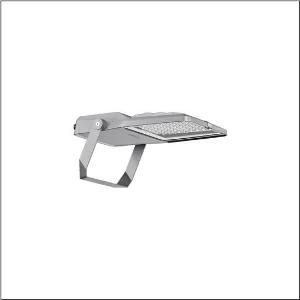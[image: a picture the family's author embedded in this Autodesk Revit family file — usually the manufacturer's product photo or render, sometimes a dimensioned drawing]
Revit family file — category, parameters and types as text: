
# Revit family: floodlight_fl_21_iq_mini___pl52_5xa7772c2d1a_8042
name_source: partatom
category: Lighting Fixtures
units: mm (PartAtom-declared; Revit-internal decimal feet)

## family parameters
Cut with Voids When Loaded = No
Host = Face
Light Source = No
Part Type = Normal
Room Calculation Point = No
Round Connector Dimension = Use Diameter
Shared = No

## types (1)
- --- (1 x LED, 12210 lm, 87.2 W, 3000K)
    Apparent Load = 87 VA
    CIE Flux Codes = 26 60 98 100 100
    Color Rendering = 70
    Color Temperature = 3000K
    Default Elevation = 1800 mm
    Description = Floodlight FL 21 iQ mini, floodlight, primary light control with lens, of PMMA, primary optical cover: protective disc, of toughened safety glass, transparent, light distribution: PL52, light emission: direct distribution, installation type: surface-mounted, LED, High Power LED, rated luminous flux: 12.210lm, luminous efficacy: 140lm/W, light colour: 730, colour temperature: 3000K, control: Street-Remote, Auto-Match, Temp-Guard, Night-Set, Smart-Wire, Desk-Remote (wireless, voltage-free reading and setting of iQ features in the workshop via application-optimized NFC function/RFID function), optimised constant luminous flux control (CLO 2.0), with terminal, 6-pole, mains connection: 220..240V, AC, 50/60Hz, start of lifetime: 87W, end of service life: 92W, reduction: 40W, luminaire housing, of diecast aluminium, powder-coated, Siteco® metallic grey (DB 702S), corrosivity category C5 mid according to DIN EN ISO 12944, sealing non-destructively replaceable, mounting bracket, of steel, galvanised, powder-coated, Siteco® metallic grey (DB 702S), protection rating (complete): IP66, insulation class (complete): insulation class II (safety insulation), certification: CE, ENEC, VDE, protection symbol: D, impact resistance: IK08, permissible operating ambient temperature: -40..+40°C, permissible operating ambient temperature for outdoor applications: -40..+50°C, standard: DIN EN 12944, LABS conformity tested according to VDMA 24364:2018-05, packaging unit: 1 piece

Light Distribution: PL52
    Height = 70 mm
    Lamp = 1 x LED
    Lamp Light Flux = 12210 lm
    Lamp Power = 87.2 W
    Lamp count = 1
    Length = 485 mm
    Luminous efficacy = 140 lm/W
    Manufacturer = Siteco
    ModVariant = No
    Model = 5XA7772C2D1A
    Number of Poles = 1
    OnlyDefault = Yes
    Power Factor = 1
    Product Name = Floodlight FL 21 iQ mini | PL52
    Product group = floodlight | pylon annexe
    ProductGroupID = 6200
    Protection Class = Protection class II
    Protection Degree = IP 66
    RLX_Detail_Level = 1
    RLX_Emergency_Light_Flux = 0 lm
    RLX_Emergency_Type = 0
    RLX_Emergency_Type_DB = No
    RlxData = <blob elided: 96513 chars, md5=54f09c59>
    Socket = socket
    Standby Power = 0 W
    System Light Flux = 12210 lm
    System Power = 87 W
    Type Comments = factory setting: luminous flux: 100 % | dim-lin: 254 | 456 mA
    Type Image = l_1006845.jpg
    URL = http://relux.com
    VarID = @adj_096675
    Voltage = 0 V
    Weight = 0.00 kg
    Width = 337 mm

## geometry (parser evidence)
native form markers: Blend x4, Sweep x13
no freeform markers — native parametric forms only
